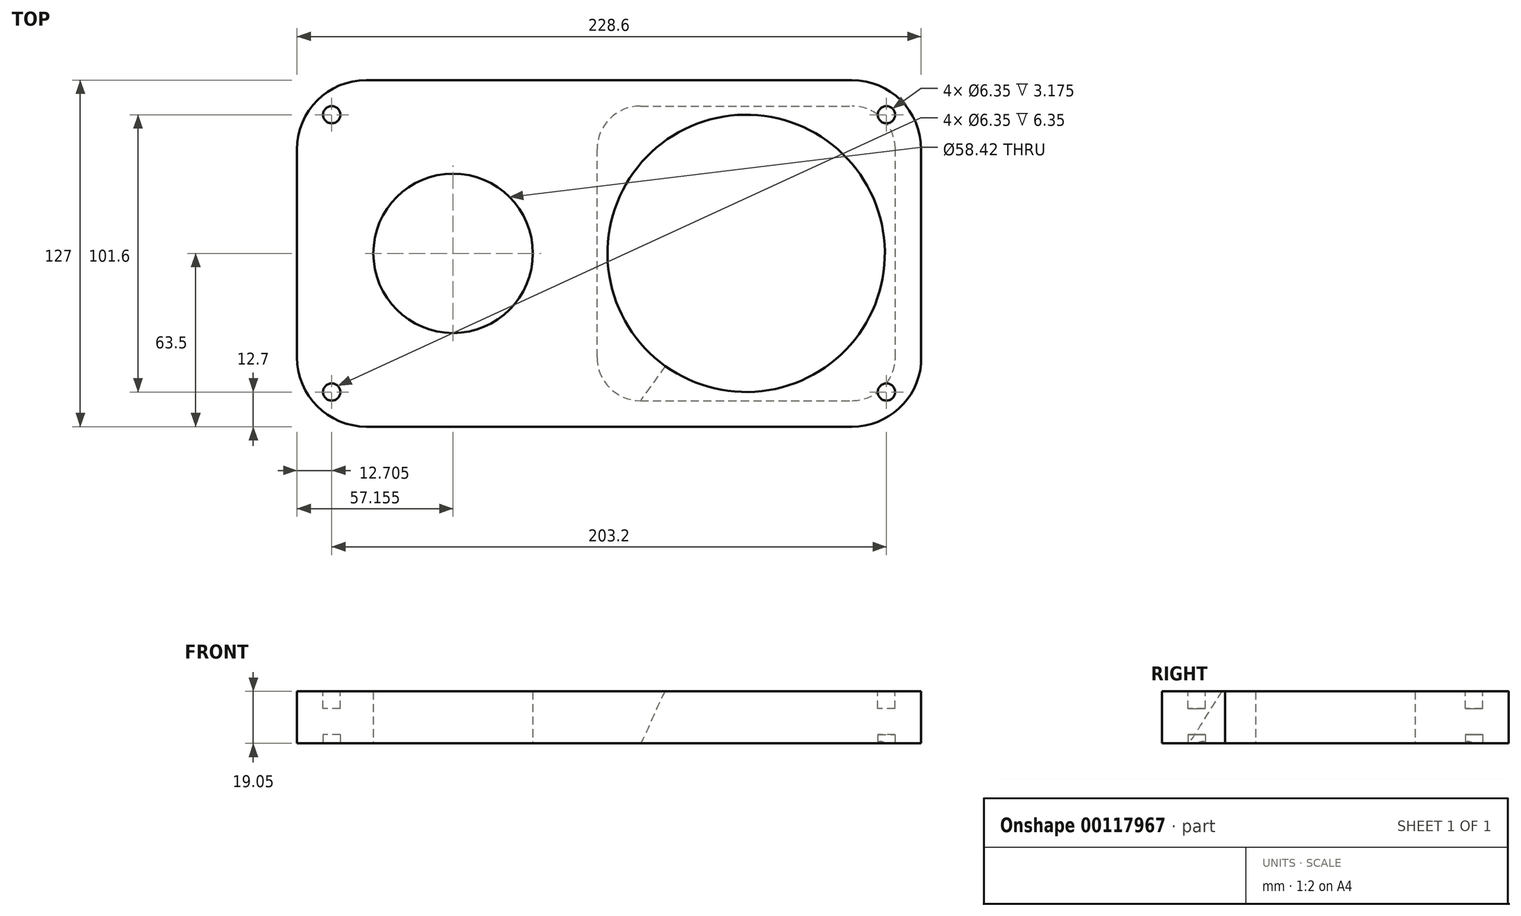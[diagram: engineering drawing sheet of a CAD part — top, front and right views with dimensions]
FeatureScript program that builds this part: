
annotation { "Feature Type Name" : "Feature", "Feature Type Description" : "" }
export const myFeature = defineFeature(function(context is Context, id is Id, definition is map)
    precondition{}
    {
        {
            var Q0;
            Q0=qCreatedBy(makeId("Top.planeOp"),FACE);
            var sketch = newSketch(context, id + "F0", { "sketchPlane" : qUnion([Q0])});
            skLineSegment(sketch, "E0.bottom", {"start": v(-139.1, 63.5) * mm, "end": v(38.7, 63.5) * mm});
            skLineSegment(sketch, "E0.top", {"start": v(-139.1, -63.5) * mm, "end": v(38.8, -63.5) * mm});
            skLineSegment(sketch, "E0.left", {"start": v(-164.5, 38.1) * mm, "end": v(-164.5, -38.1) * mm});
            skArc(sketch, "E1.filletArc", {"start": v(-139.1, 63.5) * mm, "mid": v(-157.07, 56.06) * mm, "end": v(-164.5, 38.1) * mm});
            skArc(sketch, "E2.filletArc", {"start": v(-164.5, -38.1) * mm, "mid": v(-157.07, -56.06) * mm, "end": v(-139.1, -63.5) * mm});
            skCircle(sketch, "E3", {"center": v(-107.36, 0) * mm, "radius": 29.21 * mm});
            skArc(sketch, "E4.filletArc", {"start": v(38.8, -63.5) * mm, "mid": v(55.92, -56.86) * mm, "end": v(64.1, -40.4) * mm});
            skLineSegment(sketch, "E5", {"start": v(-226.7, 50.8) * mm, "end": v(140.03, 50.8) * mm, "construction": true});
            skLineSegment(sketch, "E6", {"start": v(-224.1, -50.8) * mm, "end": v(141.89, -50.8) * mm, "construction": true});
            skLineSegment(sketch, "E7", {"start": v(-151.8, 90.06) * mm, "end": v(-151.8, -83.18) * mm, "construction": true});
            skLineSegment(sketch, "E8", {"start": v(51.4, 89.73) * mm, "end": v(51.4, -84.09) * mm, "construction": true});
            skCircle(sketch, "E9", {"center": v(-151.8, 50.8) * mm, "radius": 3.18 * mm, "construction": true});
            skCircle(sketch, "E10", {"center": v(51.4, 50.8) * mm, "radius": 3.18 * mm, "construction": true});
            skCircle(sketch, "E11", {"center": v(51.4, -50.8) * mm, "radius": 3.18 * mm, "construction": true});
            skCircle(sketch, "E12", {"center": v(-151.8, -50.8) * mm, "radius": 3.18 * mm, "construction": true});
            skLineSegment(sketch, "E13", {"start": v(-227.14, 0) * mm, "end": v(139.66, 0) * mm, "construction": true});
            skLineSegment(sketch, "E14.trimOffspring", {"start": v(64.1, 38.1) * mm, "end": v(64.1, -40.4) * mm});
            skArc(sketch, "E15.trimOffspring", {"start": v(64.1, 38.1) * mm, "mid": v(56.66, 56.06) * mm, "end": v(38.7, 63.5) * mm});
            skLineSegment(sketch, "E16", {"start": v(-50.2, 88.22) * mm, "end": v(-50.2, -93.17) * mm, "construction": true});
            skLineSegment(sketch, "E17", {"start": v(-62.9, 86.4) * mm, "end": v(-62.9, -85.21) * mm, "construction": true});
            skLineSegment(sketch, "E18.bottom", {"start": v(-50.2, 50.8) * mm, "end": v(44.54, 50.8) * mm});
            skPoint(sketch, "E19.visualSharp", {"position": v(-49.5, 49.15) * mm});
            skPoint(sketch, "E20.visualSharp", {"position": v(49.27, 49.15) * mm});
            skPoint(sketch, "E21.visualSharp", {"position": v(49.27, -48.8) * mm});
            skPoint(sketch, "E22.visualSharp", {"position": v(-49.5, -48.8) * mm});
            skCircle(sketch, "E23", {"center": v(0, 0) * mm, "radius": 50.8 * mm, "construction": true});
            skLineSegment(sketch, "E24.bottom", {"start": v(38.74, 53.97) * mm, "end": v(-38.74, 53.98) * mm, "construction": true});
            skLineSegment(sketch, "E24.top", {"start": v(38.73, -53.98) * mm, "end": v(-38.74, -53.97) * mm, "construction": true});
            skLineSegment(sketch, "E24.left", {"start": v(54.61, 38.1) * mm, "end": v(54.6, -38.1) * mm, "construction": true});
            skLineSegment(sketch, "E24.right", {"start": v(-54.61, 38.1) * mm, "end": v(-54.61, -38.1) * mm, "construction": true});
            skPoint(sketch, "E25.visualSharp", {"position": v(-54.6, 53.98) * mm});
            skArc(sketch, "E25.filletArc", {"start": v(-38.74, 53.98) * mm, "mid": v(-49.96, 49.33) * mm, "end": v(-54.61, 38.1) * mm, "construction": true});
            skPoint(sketch, "E26.visualSharp", {"position": v(54.61, 53.97) * mm});
            skArc(sketch, "E26.filletArc", {"start": v(54.61, 38.1) * mm, "mid": v(49.96, 49.33) * mm, "end": v(38.74, 53.97) * mm, "construction": true});
            skPoint(sketch, "E27.visualSharp", {"position": v(54.6, -53.98) * mm});
            skArc(sketch, "E27.filletArc", {"start": v(38.73, -53.98) * mm, "mid": v(49.96, -49.33) * mm, "end": v(54.6, -38.1) * mm, "construction": true});
            skPoint(sketch, "E28.visualSharp", {"position": v(-54.61, -53.97) * mm});
            skArc(sketch, "E28.filletArc", {"start": v(-54.61, -38.1) * mm, "mid": v(-49.96, -49.33) * mm, "end": v(-38.74, -53.98) * mm, "construction": true});
            skSolve(sketch);
        }
        {
            var Q0;
            Q0=qSketchRegion(id+"F0",true);
            extrude(context, id + "F8", {"entities" : qUnion([Q0]), "depth" : 19.05 * mm});
        }
        {
            var Q0;
            Q0=makeQuery(id+"F0.imprint","IMPRINT",FACE,{"disambiguationData":[TD([[makeQuery(id+"F0.imprint","IMPRINT",EDGE,{"derivedFrom":sQuery(id+"F0.wireOp",EDGE,"E0.bottom")}),-1.0]])]});
            var sketch = newSketch(context, id + "F1", { "sketchPlane" : qUnion([Q0])});
            skCircle(sketch, "E29", {"center": v(-151.8, -50.8) * mm, "radius": 3.18 * mm});
            skCircle(sketch, "E30", {"center": v(51.4, -50.8) * mm, "radius": 3.18 * mm});
            skCircle(sketch, "E31", {"center": v(51.4, 50.8) * mm, "radius": 3.18 * mm});
            skCircle(sketch, "E32", {"center": v(-151.8, 50.8) * mm, "radius": 3.18 * mm});
            skSolve(sketch);
        }
        {
            var Q0;
            Q0=qSketchRegion(id+"F1",true);
            extrude(context, id + "F2", {"entities" : qUnion([Q0]), "operationType" : NewBodyOperationType.REMOVE, "depth" : 3.17 * mm});
        }
        {
            var Q0;
            Q0=makeQuery(id+"F8.opExtrude","CAP_FACE",FACE,{"disambiguationData":[OSD([sQuery(id+"F0.wireOp",EDGE,"E0.bottom"),sQuery(id+"F0.wireOp",EDGE,"E0.top"),sQuery(id+"F0.wireOp",EDGE,"E0.left"),sQuery(id+"F0.wireOp",EDGE,"E1.filletArc"),sQuery(id+"F0.wireOp",EDGE,"E2.filletArc"),sQuery(id+"F0.wireOp",EDGE,"E3"),sQuery(id+"F0.wireOp",EDGE,"E4.filletArc"),sQuery(id+"F0.wireOp",EDGE,"E14.trimOffspring"),sQuery(id+"F0.wireOp",EDGE,"E15.trimOffspring"),sQuery(id+"F0.wireOp",EDGE,"7VYL7I8c-dPoo-K5Je-aqVb-YWWaIIDTXisc.bottom"),sQuery(id+"F0.wireOp",EDGE,"7VYL7I8c-dPoo-K5Je-aqVb-YWWaIIDTXisc.top"),sQuery(id+"F0.wireOp",EDGE,"7VYL7I8c-dPoo-K5Je-aqVb-YWWaIIDTXisc.left"),sQuery(id+"F0.wireOp",EDGE,"7VYL7I8c-dPoo-K5Je-aqVb-YWWaIIDTXisc.right"),sQuery(id+"F0.wireOp",EDGE,"E19.filletArc"),sQuery(id+"F0.wireOp",EDGE,"E20.filletArc"),sQuery(id+"F0.wireOp",EDGE,"E21.filletArc"),sQuery(id+"F0.wireOp",EDGE,"E22.filletArc")])],"isStart":false});
            var sketch = newSketch(context, id + "F3", { "sketchPlane" : qUnion([Q0])});
            skCircle(sketch, "E33", {"center": v(-151.8, 50.8) * mm, "radius": 3.18 * mm});
            skCircle(sketch, "E34", {"center": v(51.4, 50.8) * mm, "radius": 3.18 * mm});
            skCircle(sketch, "E35", {"center": v(51.4, -50.8) * mm, "radius": 3.18 * mm});
            skCircle(sketch, "E36", {"center": v(-151.8, -50.8) * mm, "radius": 3.18 * mm});
            skSolve(sketch);
        }
        {
            var Q0;
            Q0=qSketchRegion(id+"F3",true);
            extrude(context, id + "F4", {"entities" : qUnion([Q0]), "operationType" : NewBodyOperationType.REMOVE, "oppositeDirection" : true, "depth" : 6.35 * mm});
        }
        {
            var Q0;
            Q0=makeQuery(id+"F8.opExtrude","CAP_FACE",FACE,{"disambiguationData":[OSD([sQuery(id+"F0.wireOp",EDGE,"E0.bottom"),sQuery(id+"F0.wireOp",EDGE,"E0.top"),sQuery(id+"F0.wireOp",EDGE,"E0.left"),sQuery(id+"F0.wireOp",EDGE,"E1.filletArc"),sQuery(id+"F0.wireOp",EDGE,"E2.filletArc"),sQuery(id+"F0.wireOp",EDGE,"E3"),sQuery(id+"F0.wireOp",EDGE,"E4.filletArc"),sQuery(id+"F0.wireOp",EDGE,"E14.trimOffspring"),sQuery(id+"F0.wireOp",EDGE,"E15.trimOffspring")])],"isStart":false});
            var sketch = newSketch(context, id + "F5", { "sketchPlane" : qUnion([Q0])});
            skPoint(sketch, "E37.visualSharp", {"position": v(-47.63, 47.63) * mm});
            skPoint(sketch, "E38.visualSharp", {"position": v(47.63, 47.63) * mm});
            skPoint(sketch, "E39.visualSharp", {"position": v(47.63, -47.63) * mm});
            skPoint(sketch, "E40.visualSharp", {"position": v(-47.63, -47.63) * mm});
            skCircle(sketch, "E41", {"center": v(0, 0) * mm, "radius": 50.8 * mm});
            skSolve(sketch);
        }
        {
            var Q0;
            Q0=makeQuery(id+"F0.imprint","IMPRINT",FACE,{"disambiguationData":[TD([[makeQuery(id+"F0.imprint","IMPRINT",EDGE,{"derivedFrom":sQuery(id+"F0.wireOp",EDGE,"E0.bottom")}),-1.0]])]});
            var sketch = newSketch(context, id + "F6", { "sketchPlane" : qUnion([Q0])});
            skLineSegment(sketch, "E42.bottom", {"start": v(-38.74, -53.98) * mm, "end": v(38.73, -53.98) * mm});
            skLineSegment(sketch, "E42.top", {"start": v(-38.74, 53.98) * mm, "end": v(38.74, 53.98) * mm});
            skLineSegment(sketch, "E42.left", {"start": v(-54.61, -38.1) * mm, "end": v(-54.61, 38.1) * mm});
            skLineSegment(sketch, "E42.right", {"start": v(54.61, -38.1) * mm, "end": v(54.6, 38.1) * mm});
            skPoint(sketch, "E43.visualSharp", {"position": v(-54.61, -53.98) * mm});
            skArc(sketch, "E43.filletArc", {"start": v(-54.61, -38.1) * mm, "mid": v(-49.96, -49.33) * mm, "end": v(-38.74, -53.98) * mm});
            skPoint(sketch, "E44.visualSharp", {"position": v(54.61, -53.98) * mm});
            skArc(sketch, "E44.filletArc", {"start": v(38.73, -53.98) * mm, "mid": v(49.96, -49.33) * mm, "end": v(54.6, -38.1) * mm});
            skPoint(sketch, "E45.visualSharp", {"position": v(54.6, 53.98) * mm});
            skArc(sketch, "E45.filletArc", {"start": v(54.61, 38.1) * mm, "mid": v(49.96, 49.33) * mm, "end": v(38.74, 53.97) * mm});
            skPoint(sketch, "E46.visualSharp", {"position": v(-54.61, 53.98) * mm});
            skArc(sketch, "E46.filletArc", {"start": v(-38.74, 53.98) * mm, "mid": v(-49.96, 49.33) * mm, "end": v(-54.61, 38.1) * mm});
            skSolve(sketch);
        }
        {
            var Q1;
            Q1 = qSketchRegion(id + "F5", true);
            var Q2;
            Q2 = qSketchRegion(id + "F6", true);
            loft(context, id + "F7", {"operationType" : NewBodyOperationType.REMOVE, "startCondition" : LoftEndDerivativeType.TANGENT_TO_PROFILE, "startMagnitude" : .25, "endCondition" : LoftEndDerivativeType.TANGENT_TO_PROFILE, "endMagnitude" : .25, "sheetProfilesArray" : [{ "sheetProfileEntities" : qUnion([Q1]) }, { "sheetProfileEntities" : qUnion([Q2]) }]});
        }
    });
